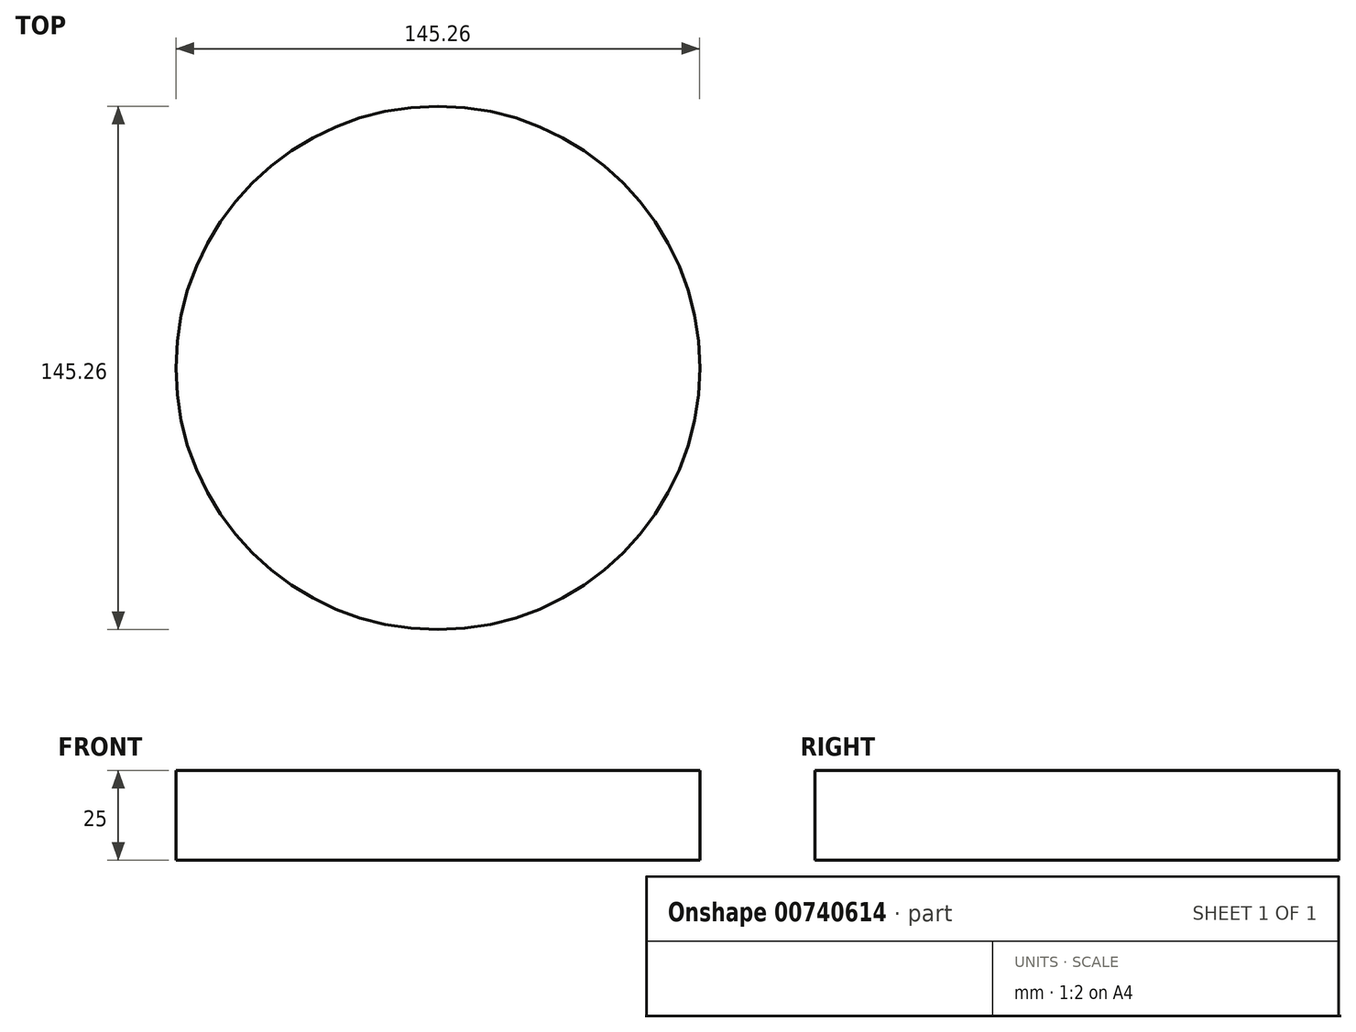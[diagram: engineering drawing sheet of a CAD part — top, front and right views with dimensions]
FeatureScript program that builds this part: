
annotation { "Feature Type Name" : "Feature", "Feature Type Description" : "" }
export const myFeature = defineFeature(function(context is Context, id is Id, definition is map)
    precondition{}
    {
        {
            var Q0;
            Q0=qCreatedBy(makeId("Top.planeOp"),FACE);
            var sketch = newSketch(context, id + "F0", { "sketchPlane" : qUnion([Q0])});
            skCircle(sketch, "E0", {"center": v(0, 0) * mm, "radius": 72.63 * mm});
            skSolve(sketch);
        }
        {
            var Q0;
            Q0=makeQuery(id+"F0.imprint","IMPRINT",FACE,{"disambiguationData":[TD([[makeQuery(id+"F0.imprint","IMPRINT",EDGE,{"derivedFrom":sQuery(id+"F0.wireOp",EDGE,"E0")}),1.0]])]});
            extrude(context, id + "F1", {"entities" : qUnion([Q0]), "depth" : 25 * mm, "offsetDistance" : 25 * mm, "hasDraft" : true, "draftAngle" : 0 * degree});
        }
        {
            var Q0;
            Q0=makeQuery(id+"F1.opExtrude","CAP_FACE",FACE,{"disambiguationData":[OSD([sQuery(id+"F0.wireOp",EDGE,"E0")])],"isStart":false});
            var sketch = newSketch(context, id + "F2", { "sketchPlane" : qUnion([Q0])});
            skCircle(sketch, "E1.0", {"center": v(0, 0) * mm, "radius": 72.63 * mm});
            skLineSegment(sketch, "E2", {"start": v(0, -72.63) * mm, "end": v(0, 72.63) * mm});
            skSolve(sketch);
        }
        {
            var Q0;
            Q0=qCreatedBy(makeId("Right.planeOp"),FACE);
            var sketch = newSketch(context, id + "F3", { "sketchPlane" : qUnion([Q0])});
            skLineSegment(sketch, "E3", {"start": v(-72.63, 25) * mm, "end": v(-72.63, 165) * mm});
            skLineSegment(sketch, "E4", {"start": v(-12.63, 225) * mm, "end": v(0, 225) * mm});
            skPoint(sketch, "E5.visualSharp", {"position": v(-72.63, 225) * mm});
            skArc(sketch, "E5.filletArc", {"start": v(-12.63, 225) * mm, "mid": v(-55.06, 207.43) * mm, "end": v(-72.63, 165) * mm});
            skSolve(sketch);
        }
        {
            var Q0;
            {var subQ0=sQuery(id+"F2.wireOp",EDGE,"E2");Q0=makeQuery(id+"F2.imprint","IMPRINT",FACE,{"disambiguationData":[TD([[makeQuery(id+"F2.imprint","IMPRINT",EDGE,{"derivedFrom":subQ0}),1.0]])]});}
            var sketch = newSketch(context, id + "F4", { "sketchPlane" : qUnion([Q0])});
            skCircle(sketch, "E6", {"center": v(0, -69.5) * mm, "radius": 1.75 * mm});
            skSolve(sketch);
        }
    });
